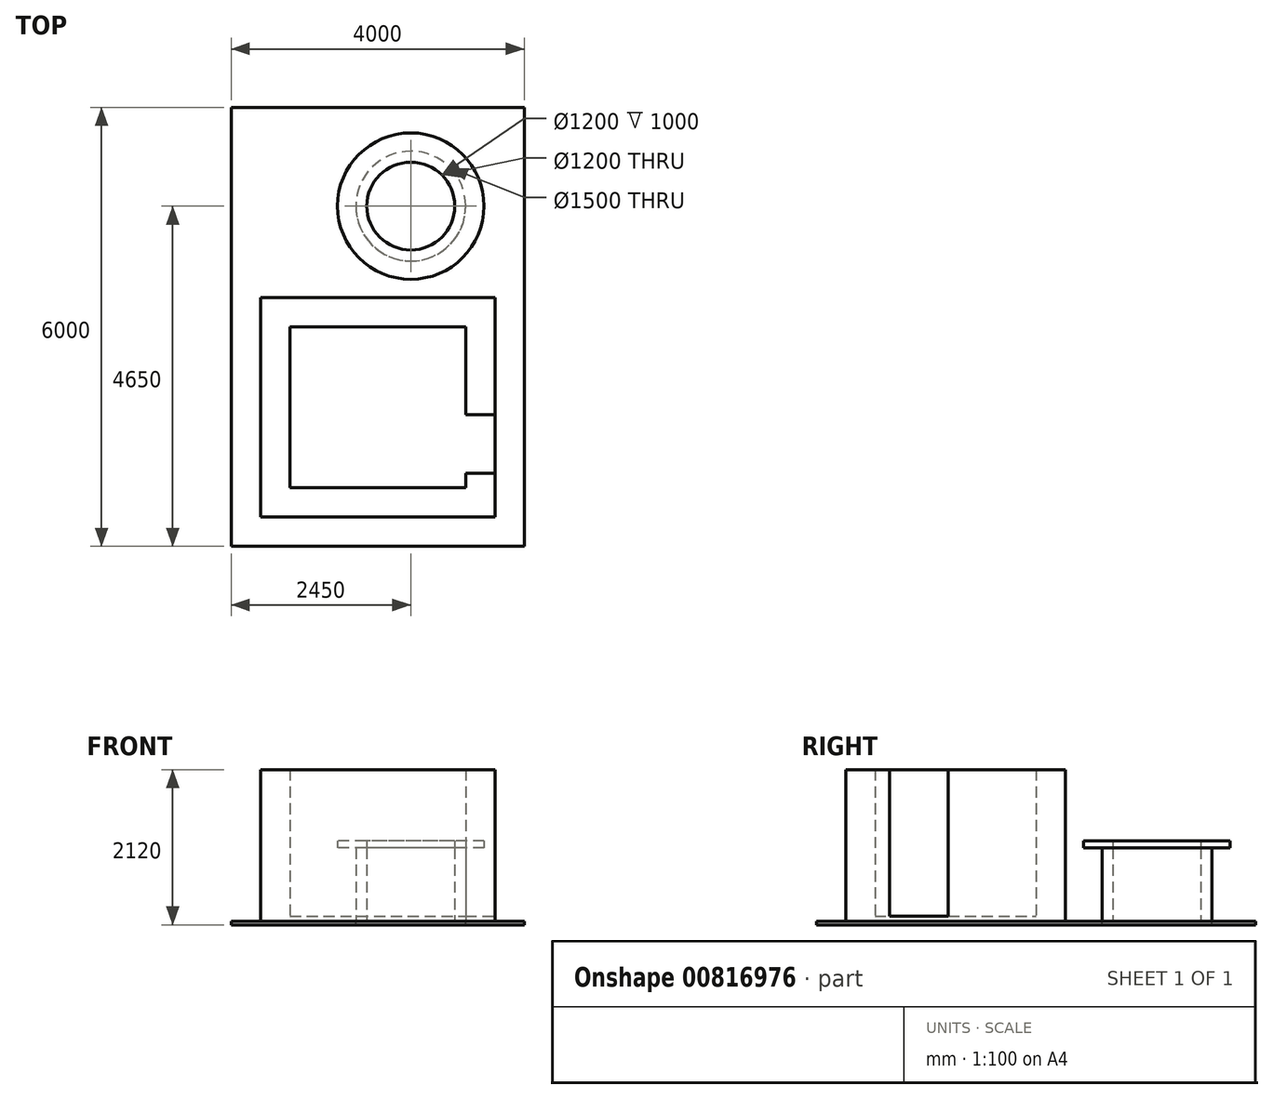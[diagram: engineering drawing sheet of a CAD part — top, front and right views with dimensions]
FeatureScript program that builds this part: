
annotation { "Feature Type Name" : "Feature", "Feature Type Description" : "" }
export const myFeature = defineFeature(function(context is Context, id is Id, definition is map)
    precondition{}
    {
        {
            var Q0;
            Q0=qCreatedBy(makeId("Top.planeOp"),FACE);
            var sketch = newSketch(context, id + "F0", { "sketchPlane" : qUnion([Q0])});
            skLineSegment(sketch, "E0.bottom", {"start": v(-1600, -1500) * mm, "end": v(1600, -1500) * mm});
            skLineSegment(sketch, "E0.top", {"start": v(-1600, 1500) * mm, "end": v(1600, 1500) * mm});
            skLineSegment(sketch, "E0.left", {"start": v(-1600, -1500) * mm, "end": v(-1600, 1500) * mm});
            skLineSegment(sketch, "E0.right", {"start": v(1600, -1500) * mm, "end": v(1600, 1500) * mm});
            skPoint(sketch, "E0.middle", {"position": v(0, 0) * mm});
            skSolve(sketch);
        }
        {
            var Q0;
            Q0 = qSketchRegion(id + "F0", true);
            extrude(context, id + "F1", {"entities" : qUnion([Q0]), "depth" : 70 * mm, "offsetDistance" : 25 * mm});
        }
        {
            var Q0;
            Q0=makeQuery(id+"F1.opExtrude","CAP_FACE",FACE,{"disambiguationData":[OSD([sQuery(id+"F0.wireOp",EDGE,"E0.bottom"),sQuery(id+"F0.wireOp",EDGE,"E0.top"),sQuery(id+"F0.wireOp",EDGE,"E0.left"),sQuery(id+"F0.wireOp",EDGE,"E0.right")])],"isStart":false});
            var sketch = newSketch(context, id + "F2", { "sketchPlane" : qUnion([Q0])});
            skLineSegment(sketch, "E1.bottom", {"start": v(-1200, -1100) * mm, "end": v(1200, -1100) * mm});
            skLineSegment(sketch, "E1.top", {"start": v(-1200, 1100) * mm, "end": v(1200, 1100) * mm});
            skLineSegment(sketch, "E1.left", {"start": v(-1200, -1100) * mm, "end": v(-1200, 1100) * mm});
            skLineSegment(sketch, "E1.right", {"start": v(1200, -1100) * mm, "end": v(1200, -900) * mm});
            skPoint(sketch, "E1.middle", {"position": v(0, 0) * mm});
            skLineSegment(sketch, "E2", {"start": v(1200, -900) * mm, "end": v(1600, -900) * mm});
            skLineSegment(sketch, "E3", {"start": v(1200, -100) * mm, "end": v(1600, -100) * mm});
            skLineSegment(sketch, "E4.0", {"start": v(1600, -1500) * mm, "end": v(1600, -900) * mm});
            skLineSegment(sketch, "E5.0.0", {"start": v(1600, 1500) * mm, "end": v(-1600, 1500) * mm});
            skLineSegment(sketch, "E5.0.1", {"start": v(-1600, 1500) * mm, "end": v(-1600, -1500) * mm});
            skLineSegment(sketch, "E5.0.2", {"start": v(-1600, -1500) * mm, "end": v(1600, -1500) * mm});
            skLineSegment(sketch, "E5.0.3", {"start": v(1600, -1500) * mm, "end": v(1600, 1500) * mm});
            skLineSegment(sketch, "E6.trimOffspring", {"start": v(1200, -100) * mm, "end": v(1200, 1100) * mm});
            skLineSegment(sketch, "E7.trimOffspring", {"start": v(1600, -100) * mm, "end": v(1600, 1500) * mm});
            skSolve(sketch);
        }
        {
            var Q0;
            Q0=makeQuery(id+"F2.imprint","IMPRINT",FACE,{"disambiguationData":[TD([[makeQuery(id+"F2.imprint","IMPRINT",EDGE,{"derivedFrom":sQuery(id+"F2.wireOp",EDGE,"E1.bottom")}),-1.0]])]});
            extrude(context, id + "F3", {"entities" : qUnion([Q0]), "operationType" : NewBodyOperationType.ADD, "depth" : 2000 * mm, "offsetDistance" : 25 * mm});
        }
        {
            var Q0;
            Q0=makeQuery(id+"F1.opExtrude","CAP_FACE",FACE,{"disambiguationData":[OSD([sQuery(id+"F0.wireOp",EDGE,"E0.bottom"),sQuery(id+"F0.wireOp",EDGE,"E0.top"),sQuery(id+"F0.wireOp",EDGE,"E0.left"),sQuery(id+"F0.wireOp",EDGE,"E0.right")])],"isStart":true});
            var sketch = newSketch(context, id + "F4", { "sketchPlane" : qUnion([Q0])});
            skLineSegment(sketch, "E8.bottom", {"start": v(2000, 1900) * mm, "end": v(-2000, 1900) * mm});
            skLineSegment(sketch, "E8.top", {"start": v(2000, -4100) * mm, "end": v(-2000, -4100) * mm});
            skLineSegment(sketch, "E8.left", {"start": v(2000, 1900) * mm, "end": v(2000, -4100) * mm});
            skLineSegment(sketch, "E8.right", {"start": v(-2000, 1900) * mm, "end": v(-2000, -4100) * mm});
            skPoint(sketch, "E9", {"position": v(0, 1900) * mm});
            skSolve(sketch);
        }
        {
            var Q0;
            Q0 = qSketchRegion(id + "F4", true);
            extrude(context, id + "F5", {"entities" : qUnion([Q0]), "depth" : 50 * mm, "offsetDistance" : 25 * mm});
        }
        {
            var Q0;
            Q0=makeQuery(id+"F5.opExtrude","CAP_FACE",FACE,{"disambiguationData":[OSD([sQuery(id+"F4.wireOp",EDGE,"E8.bottom"),sQuery(id+"F4.wireOp",EDGE,"E8.top"),sQuery(id+"F4.wireOp",EDGE,"E8.left"),sQuery(id+"F4.wireOp",EDGE,"E8.right")])],"isStart":true});
            var sketch = newSketch(context, id + "F6", { "sketchPlane" : qUnion([Q0])});
            skCircle(sketch, "E10", {"center": v(450, 2750) * mm, "radius": 750 * mm});
            skSolve(sketch);
        }
        {
            var Q0;
            Q0 = qSketchRegion(id + "F6", true);
            extrude(context, id + "F7", {"entities" : qUnion([Q0]), "operationType" : NewBodyOperationType.REMOVE, "oppositeDirection" : true, "depth" : 500 * mm, "offsetDistance" : 25 * mm});
        }
        {
            var Q0;
            Q0 = qSketchRegion(id + "F6", true);
            extrude(context, id + "F8", {"entities" : qUnion([Q0]), "depth" : 1000 * mm, "offsetDistance" : 25 * mm});
        }
        {
            var Q0;
            Q0=makeQuery(id+"F8.opExtrude","CAP_FACE",FACE,{"disambiguationData":[OSD([sQuery(id+"F6.wireOp",EDGE,"E10")])],"isStart":false});
            var sketch = newSketch(context, id + "F9", { "sketchPlane" : qUnion([Q0])});
            skCircle(sketch, "E11", {"center": v(450, 2750) * mm, "radius": 1000 * mm});
            skSolve(sketch);
        }
        {
            var Q0;
            Q0 = qSketchRegion(id + "F9", true);
            extrude(context, id + "F10", {"entities" : qUnion([Q0]), "depth" : 100 * mm, "offsetDistance" : 25 * mm});
        }
        {
            var Q0;
            Q0=makeQuery(id+"F8.opExtrude","CAP_FACE",FACE,{"disambiguationData":[OSD([sQuery(id+"F6.wireOp",EDGE,"E10")])],"isStart":true});
            var sketch = newSketch(context, id + "F11", { "sketchPlane" : qUnion([Q0])});
            skCircle(sketch, "E12", {"center": v(450, -2750) * mm, "radius": 600 * mm});
            skSolve(sketch);
        }
        {
            var Q0;
            Q0 = qSketchRegion(id + "F11", true);
            extrude(context, id + "F12", {"entities" : qUnion([Q0]), "operationType" : NewBodyOperationType.REMOVE, "endBound" : BoundingType.THROUGH_ALL, "oppositeDirection" : true, "depth" : 25 * mm, "offsetDistance" : 25 * mm});
        }
    });
